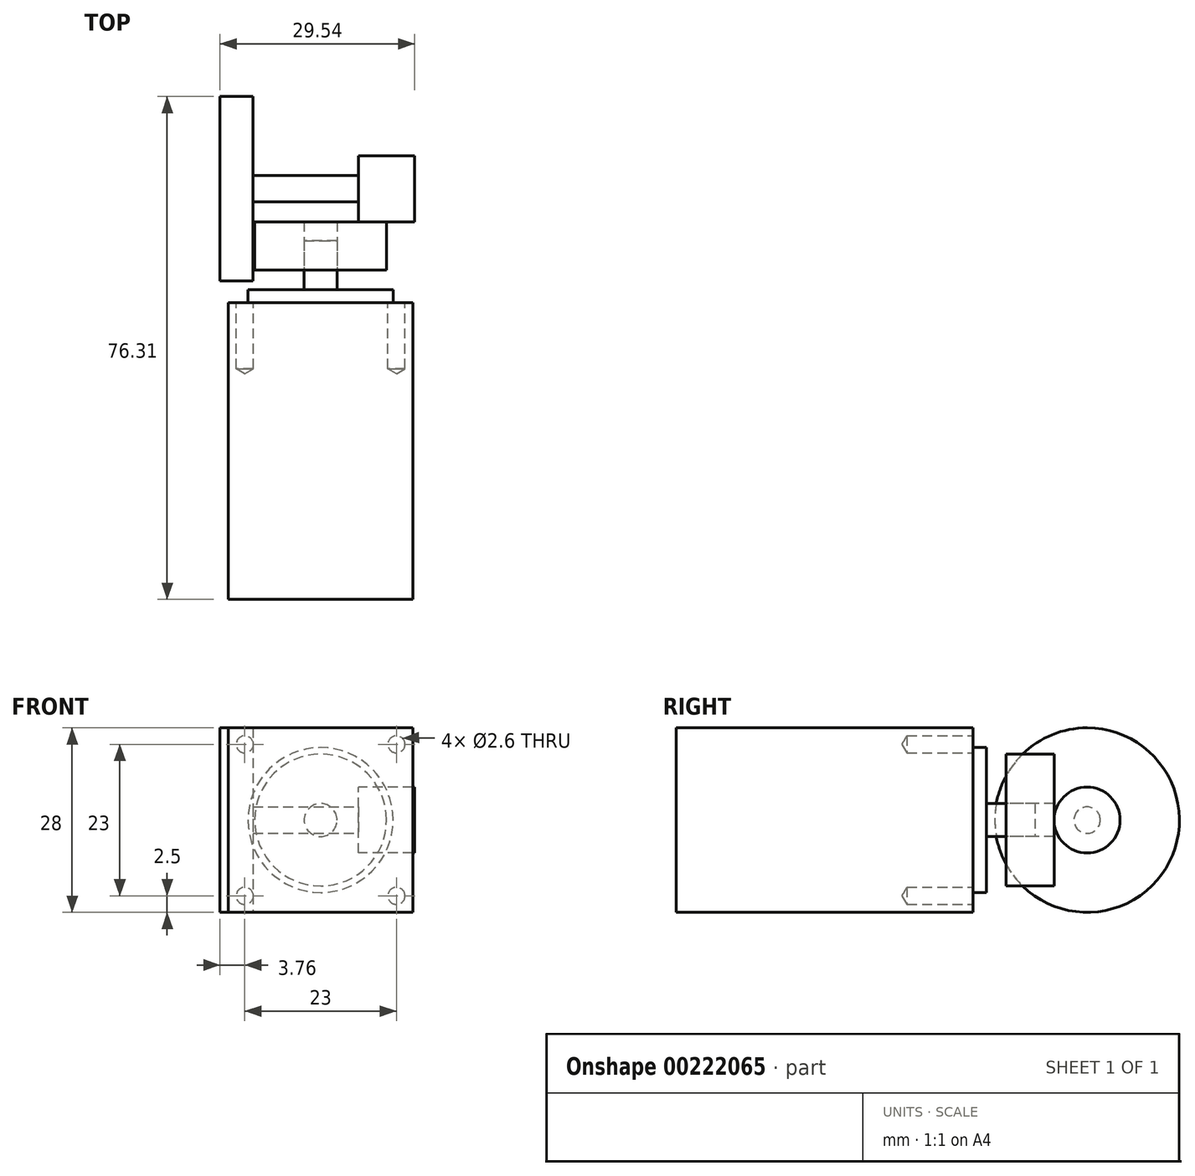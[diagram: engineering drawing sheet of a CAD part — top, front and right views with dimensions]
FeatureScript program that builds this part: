
annotation { "Feature Type Name" : "Feature", "Feature Type Description" : "" }
export const myFeature = defineFeature(function(context is Context, id is Id, definition is map)
    precondition{}
    {
        {
            var Q0;
            Q0=qCreatedBy(makeId("Front.planeOp"),FACE);
            var sketch = newSketch(context, id + "F0", { "sketchPlane" : qUnion([Q0])});
            skLineSegment(sketch, "E0.bottom", {"start": v(14, -14) * mm, "end": v(-14, -14) * mm});
            skLineSegment(sketch, "E0.top", {"start": v(14, 14) * mm, "end": v(-14, 14) * mm});
            skLineSegment(sketch, "E0.left", {"start": v(14, -14) * mm, "end": v(14, 14) * mm});
            skLineSegment(sketch, "E0.right", {"start": v(-14, -14) * mm, "end": v(-14, 14) * mm});
            skPoint(sketch, "E0.middle", {"position": v(0, 0) * mm});
            skSolve(sketch);
        }
        {
            var Q0;
            Q0=makeQuery(id+"F0.imprint","IMPRINT",FACE,{"disambiguationData":[TD([[makeQuery(id+"F0.imprint","IMPRINT",EDGE,{"derivedFrom":sQuery(id+"F0.wireOp",EDGE,"E0.bottom")}),-1.0]])]});
            extrude(context, id + "F1", {"entities" : qUnion([Q0]), "depth" : 45 * mm, "offsetDistance" : 25 * mm});
        }
        {
            var Q0;
            Q0=makeQuery(id+"F1.opExtrude","CAP_FACE",FACE,{"disambiguationData":[OSD([sQuery(id+"F0.wireOp",EDGE,"E0.bottom"),sQuery(id+"F0.wireOp",EDGE,"E0.top"),sQuery(id+"F0.wireOp",EDGE,"E0.left"),sQuery(id+"F0.wireOp",EDGE,"E0.right")])],"isStart":true});
            var sketch = newSketch(context, id + "F2", { "sketchPlane" : qUnion([Q0])});
            skCircle(sketch, "E1", {"center": v(0, 0) * mm, "radius": 11 * mm});
            skSolve(sketch);
        }
        {
            var Q0;
            Q0=makeQuery(id+"F2.imprint","IMPRINT",FACE,{"disambiguationData":[TD([[makeQuery(id+"F2.imprint","IMPRINT",EDGE,{"derivedFrom":sQuery(id+"F2.wireOp",EDGE,"E1")}),1.0]])]});
            extrude(context, id + "F3", {"entities" : qUnion([Q0]), "operationType" : NewBodyOperationType.ADD, "depth" : 2 * mm, "offsetDistance" : 25 * mm});
        }
        {
            var Q0;
            Q0=makeQuery(id+"F1.opExtrude","CAP_FACE",FACE,{"disambiguationData":[OSD([sQuery(id+"F0.wireOp",EDGE,"E0.bottom"),sQuery(id+"F0.wireOp",EDGE,"E0.top"),sQuery(id+"F0.wireOp",EDGE,"E0.left"),sQuery(id+"F0.wireOp",EDGE,"E0.right")])],"isStart":true});
            var sketch = newSketch(context, id + "F4", { "sketchPlane" : qUnion([Q0])});
            skLineSegment(sketch, "E2.bottom", {"start": v(11.5, 11.5) * mm, "end": v(-11.5, 11.5) * mm, "construction": true});
            skLineSegment(sketch, "E2.top", {"start": v(11.5, -11.5) * mm, "end": v(-11.5, -11.5) * mm, "construction": true});
            skLineSegment(sketch, "E2.left", {"start": v(11.5, 11.5) * mm, "end": v(11.5, -11.5) * mm, "construction": true});
            skLineSegment(sketch, "E2.right", {"start": v(-11.5, 11.5) * mm, "end": v(-11.5, -11.5) * mm, "construction": true});
            skPoint(sketch, "E2.middle", {"position": v(0, 0) * mm});
            skPoint(sketch, "E3", {"position": v(-11.5, 11.5) * mm});
            skPoint(sketch, "E4", {"position": v(11.5, 11.5) * mm});
            skPoint(sketch, "E5", {"position": v(11.5, -11.5) * mm});
            skPoint(sketch, "E6", {"position": v(-11.5, -11.5) * mm});
            skSolve(sketch);
        }
        {
            var Q0;
            Q0=sQuery(id+"F4.wireOp",VERTEX,"E3");
            var Q1;
            Q1=sQuery(id+"F4.wireOp",VERTEX,"E4");
            var Q2;
            Q2=sQuery(id+"F4.wireOp",VERTEX,"E5");
            var Q3;
            Q3=sQuery(id+"F4.wireOp",VERTEX,"E6");
            var Q4;
            Q4=makeQuery(id+"F1.opExtrude","SWEPT_BODY",BODY,{"disambiguationData":[OSD([sQuery(id+"F0.wireOp",EDGE,"E0.bottom"),sQuery(id+"F0.wireOp",EDGE,"E0.top"),sQuery(id+"F0.wireOp",EDGE,"E0.left"),sQuery(id+"F0.wireOp",EDGE,"E0.right")])]});
            hole(context, id + "F5", {"style" : HoleStyle.SIMPLE, "endStyle" : HoleEndStyle.BLIND, "holeDiameter" : 2.6 * mm, "majorDiameter" : 5 * mm, "holeDepth" : 10 * mm, "isTappedThrough" : true, "tappedDepth" : 12 * mm, "tapClearance" : 3, "locations" : qUnion([Q0, Q1, Q2, Q3]), "scope" : qUnion([Q4])});
        }
        {
            var Q0;
            Q0=makeQuery(id+"F3.opExtrude","CAP_FACE",FACE,{"disambiguationData":[OSD([sQuery(id+"F2.wireOp",EDGE,"E1")])],"isStart":false});
            var sketch = newSketch(context, id + "F6", { "sketchPlane" : qUnion([Q0])});
            skCircle(sketch, "E7", {"center": v(0, 0) * mm, "radius": 2.5 * mm});
            skSolve(sketch);
        }
        {
            var Q0;
            Q0=makeQuery(id+"F6.imprint","IMPRINT",FACE,{"disambiguationData":[TD([[makeQuery(id+"F6.imprint","IMPRINT",EDGE,{"derivedFrom":sQuery(id+"F6.wireOp",EDGE,"E7")}),1.0]])]});
            extrude(context, id + "F7", {"entities" : qUnion([Q0]), "operationType" : NewBodyOperationType.ADD, "depth" : 7.4 * mm, "offsetDistance" : 25 * mm});
        }
        {
            var Q0;
            Q0=makeQuery(id+"F3.opExtrude","CAP_FACE",FACE,{"disambiguationData":[OSD([sQuery(id+"F2.wireOp",EDGE,"E1")])],"isStart":false});
            cPlane(context, id + "F8", {"entities" : qUnion([Q0]), "cplaneType" : CPlaneType.OFFSET, "offset" : 3 * mm, "width" : 150 * mm, "height" : 150 * mm});
        }
        {
            var Q0;
            Q0=qCreatedBy(id+"F8.planeOp",FACE);
            var sketch = newSketch(context, id + "F9", { "sketchPlane" : qUnion([Q0])});
            skCircle(sketch, "E8.0", {"center": v(0, 0) * mm, "radius": 2.5 * mm});
            skCircle(sketch, "E9", {"center": v(0, 0) * mm, "radius": 10 * mm});
            skSolve(sketch);
        }
        {
            var Q0;
            Q0=makeQuery(id+"F9.imprint","IMPRINT",FACE,{"disambiguationData":[TD([[makeQuery(id+"F9.imprint","IMPRINT",EDGE,{"derivedFrom":sQuery(id+"F9.wireOp",EDGE,"E8.0")}),-1.0]])]});
            extrude(context, id + "F10", {"entities" : qUnion([Q0]), "depth" : 7.3 * mm, "offsetDistance" : 25 * mm});
        }
        {
            var Q0;
            Q0=qCreatedBy(makeId("Right.planeOp"),FACE);
            cPlane(context, id + "F11", {"entities" : qUnion([Q0]), "cplaneType" : CPlaneType.OFFSET, "offset" : 5.74 * mm, "width" : 150 * mm, "height" : 150 * mm});
        }
        {
            var Q0;
            Q0=qCreatedBy(id+"F11.planeOp",FACE);
            var sketch = newSketch(context, id + "F12", { "sketchPlane" : qUnion([Q0])});
            skCircle(sketch, "E10", {"center": v(17.3, 0) * mm, "radius": 5 * mm});
            skSolve(sketch);
        }
        {
            var Q0;
            Q0=makeQuery(id+"F12.imprint","IMPRINT",FACE,{"disambiguationData":[TD([[makeQuery(id+"F12.imprint","IMPRINT",EDGE,{"derivedFrom":sQuery(id+"F12.wireOp",EDGE,"E10")}),1.0]])]});
            extrude(context, id + "F13", {"entities" : qUnion([Q0]), "depth" : 8.54 * mm, "offsetDistance" : 25 * mm});
        }
        {
            var Q0;
            Q0=makeQuery(id+"F13.opExtrude","CAP_FACE",FACE,{"disambiguationData":[OSD([sQuery(id+"F12.wireOp",EDGE,"E10")])],"isStart":true});
            var sketch = newSketch(context, id + "F14", { "sketchPlane" : qUnion([Q0])});
            skCircle(sketch, "E11.0", {"center": v(-17.3, 0) * mm, "radius": 5 * mm});
            skCircle(sketch, "E12", {"center": v(-17.3, 0) * mm, "radius": 2 * mm});
            skSolve(sketch);
        }
        {
            var Q0;
            Q0=makeQuery(id+"F14.imprint","IMPRINT",FACE,{"disambiguationData":[TD([[makeQuery(id+"F14.imprint","IMPRINT",EDGE,{"derivedFrom":sQuery(id+"F14.wireOp",EDGE,"E12")}),1.0]])]});
            extrude(context, id + "F15", {"entities" : qUnion([Q0]), "operationType" : NewBodyOperationType.ADD, "depth" : 16 * mm, "offsetDistance" : 25 * mm});
        }
        {
            var Q0;
            Q0=makeQuery(id+"F15.opExtrude","CAP_FACE",FACE,{"disambiguationData":[OSD([sQuery(id+"F14.wireOp",EDGE,"E12")])],"isStart":false});
            var sketch = newSketch(context, id + "F16", { "sketchPlane" : qUnion([Q0])});
            skCircle(sketch, "E13", {"center": v(-17.3, 0) * mm, "radius": 14 * mm});
            skSolve(sketch);
        }
        {
            var Q0;
            Q0=makeQuery(id+"F16.imprint","IMPRINT",FACE,{"disambiguationData":[TD([[makeQuery(id+"F16.imprint","IMPRINT",EDGE,{"derivedFrom":sQuery(id+"F16.wireOp",EDGE,"E13")}),1.0]])]});
            var Q1;
            Q1=makeQuery(id+"F16.imprint","IMPRINT",FACE,{"disambiguationData":[TD([[makeQuery(id+"F16.imprint","IMPRINT",EDGE,{"derivedFrom":makeQuery(id+"F15.opExtrude","CAP_EDGE",EDGE,{"disambiguationData":[OSD([sQuery(id+"F14.wireOp",EDGE,"E12")])],"isStart":false})}),1.0]])]});
            extrude(context, id + "F17", {"entities" : qUnion([Q0, Q1]), "depth" : 5 * mm, "offsetDistance" : 25 * mm});
        }
    });
